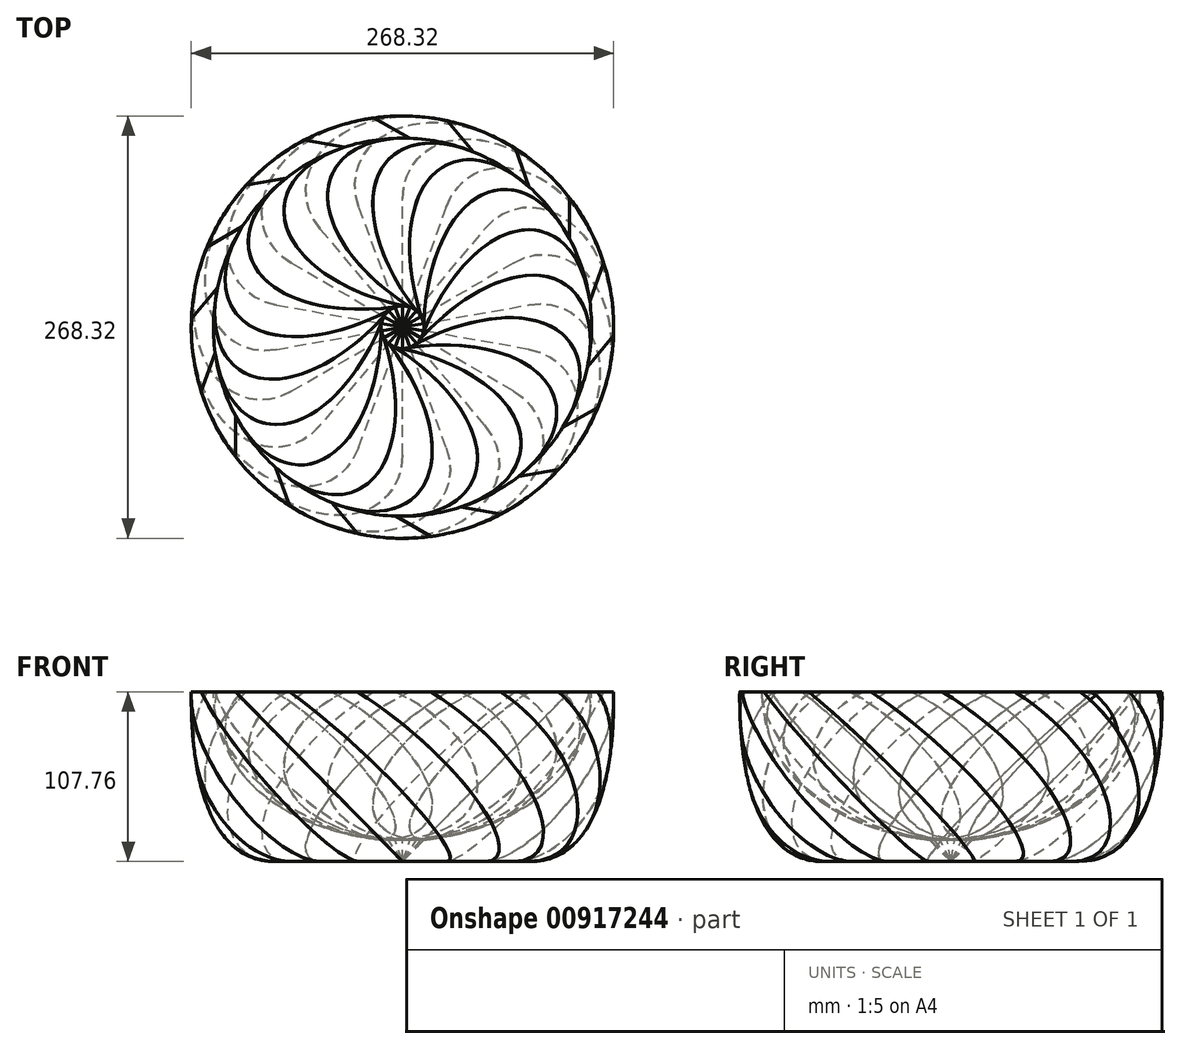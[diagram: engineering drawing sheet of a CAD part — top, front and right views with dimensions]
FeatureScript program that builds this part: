
annotation { "Feature Type Name" : "Feature", "Feature Type Description" : "" }
export const myFeature = defineFeature(function(context is Context, id is Id, definition is map)
    precondition{}
    {
        {
            var Q0;
            Q0=qCreatedBy(makeId("Top.planeOp"),FACE);
            var sketch = newSketch(context, id + "F0", { "sketchPlane" : qUnion([Q0])});
            skLineSegment(sketch, "E0", {"start": v(0, 0) * mm, "end": v(0, 0) * mm});
            skLineSegment(sketch, "E1", {"start": v(0, 0) * mm, "end": v(152.4, 26.87) * mm});
            skLineSegment(sketch, "E2", {"start": v(152.4, 26.87) * mm, "end": v(152.4, -26.87) * mm});
            skLineSegment(sketch, "E3", {"start": v(152.4, -26.87) * mm, "end": v(0, 0) * mm});
            skLineSegment(sketch, "E4", {"start": v(152.4, -26.87) * mm, "end": v(0, 0) * mm, "construction": true});
            skSolve(sketch);
        }
        {
            var Q0;
            Q0=qCreatedBy(makeId("Right.planeOp"),FACE);
            var sketch = newSketch(context, id + "F1", { "sketchPlane" : qUnion([Q0])});
            skLineSegment(sketch, "E5", {"start": v(0, 171.69) * mm, "end": v(0, 0) * mm, "construction": true});
            skLineSegment(sketch, "E6", {"start": v(0, 0) * mm, "end": v(-107.76, 107.76) * mm});
            skSolve(sketch);
        }
        {
            var Q0;
            Q0=makeQuery(id+"F0.imprint","IMPRINT",FACE,{"disambiguationData":[TD([[makeQuery(id+"F0.imprint","IMPRINT",EDGE,{"derivedFrom":sQuery(id+"F0.wireOp",EDGE,"E1")}),-1.0]])]});
            var Q1;
            Q1=sQuery(id+"F1.wireOp",EDGE,"E6");
            sweep(context, id + "F2", {"profiles" : qUnion([Q0]), "path" : qUnion([Q1]), "keepProfileOrientation" : true});
        }
        {
            var Q0;
            Q0=makeQuery(id+"F2.opSweep","SWEPT_BODY",BODY,{"disambiguationData":[OSD([sQuery(id+"F0.wireOp",EDGE,"E1"),sQuery(id+"F0.wireOp",EDGE,"E2"),sQuery(id+"F0.wireOp",EDGE,"E3"),sQuery(id+"F1.wireOp",EDGE,"D6Qg7ocj-M6jF-6LMz-4Vtr-bwkUxQN4MXTZ")])]});
            var Q1;
            Q1=sQuery(id+"F1.wireOp",EDGE,"E5");
            circularPattern(context, id + "F3", {"entities" : qUnion([Q0]), "axis" : qUnion([Q1]), "angle" : 360 * degree, "instanceCount" : 18, "equalSpace" : true});
        }
        {
            var Q0;
            Q0=qCreatedBy(makeId("Right.planeOp"),FACE);
            var sketch = newSketch(context, id + "F4", { "sketchPlane" : qUnion([Q0])});
            skPoint(sketch, "E7.0", {"position": v(5.18, 107.76) * mm});
            skLineSegment(sketch, "E8", {"start": v(237.92, 107.76) * mm, "end": v(-205.4, 107.76) * mm, "construction": true});
            skLineSegment(sketch, "E9", {"start": v(-133.77, 120.46) * mm, "end": v(-120.1, 107.76) * mm});
            skLineSegment(sketch, "E10", {"start": v(0, 0) * mm, "end": v(0, 12.7) * mm});
            skFitSpline(sketch, "E11", {"points": [v(0, 12.7) * mm, v(-120.1, 107.76) * mm], "startDerivative": vector(-212.29, 9.22) * mm, "endDerivative": vector(0, 164.8) * mm});
            skLineSegment(sketch, "E12", {"start": v(0, 0) * mm, "end": v(-81.27, 0) * mm});
            skFitSpline(sketch, "E13", {"points": [v(-81.27, 0) * mm, v(-133.77, 120.46) * mm], "startDerivative": vector(-124.5, 0) * mm, "endDerivative": vector(9.03, 196.05) * mm});
            skSolve(sketch);
        }
        {
            var Q0;
            Q0 = qSketchRegion(id + "F4", true);
            var Q1;
            Q1=sQuery(id+"F4.wireOp",EDGE,"E10");
            revolve(context, id + "F5", {"operationType" : NewBodyOperationType.INTERSECT, "surfaceOperationType" : NewSurfaceOperationType.NEW, "entities" : qUnion([Q0]), "axis" : qUnion([Q1]), "revolveType" : RevolveType.FULL, "oppositeDirection" : true});
        }
    });
